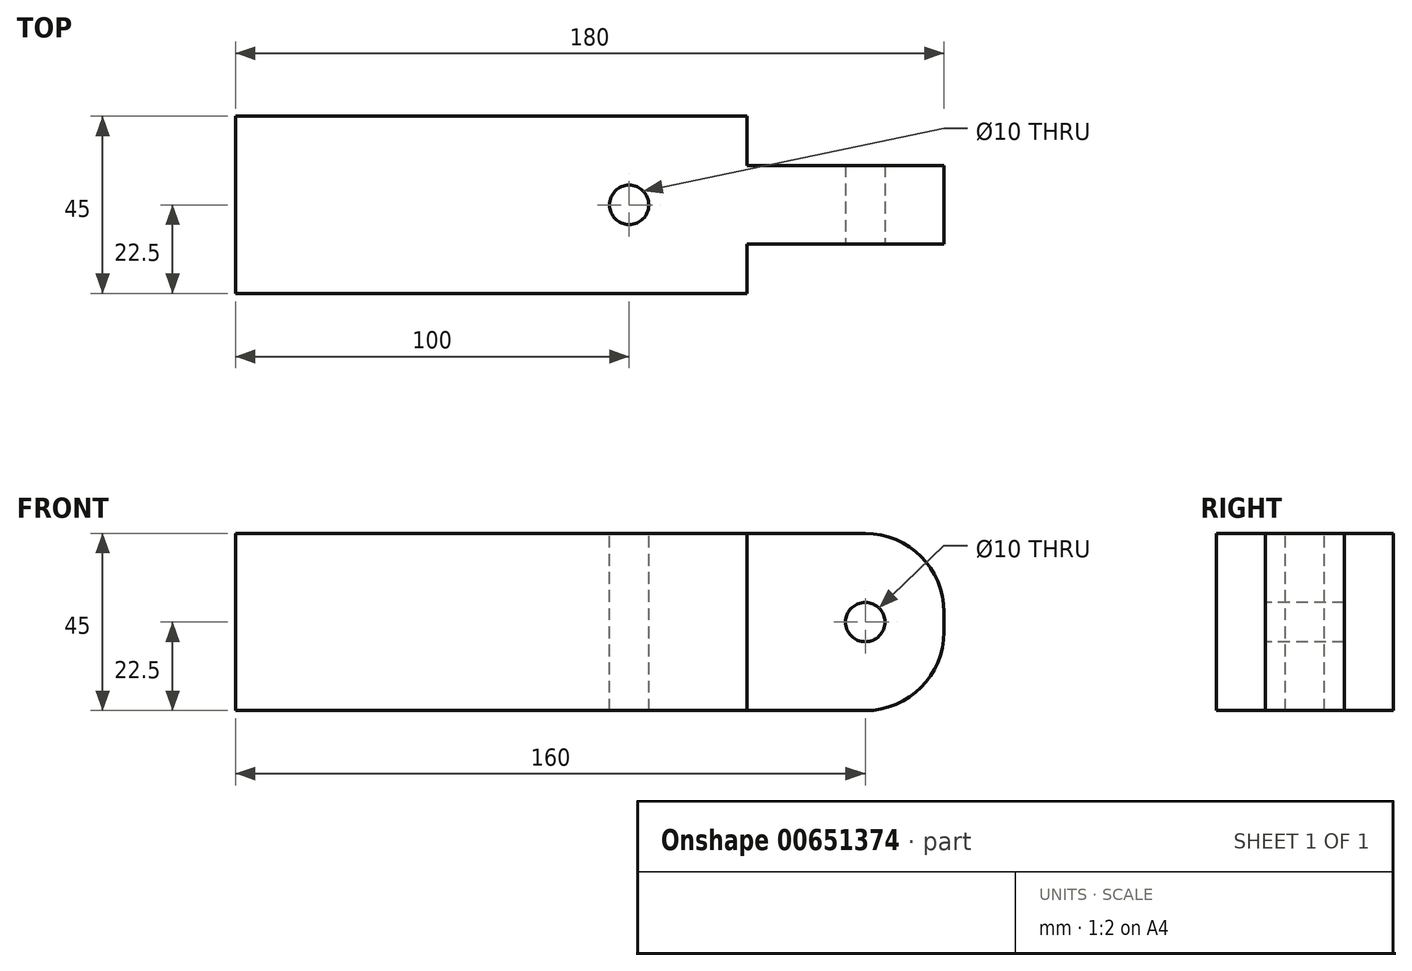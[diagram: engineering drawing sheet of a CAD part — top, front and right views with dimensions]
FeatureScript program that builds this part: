
annotation { "Feature Type Name" : "Feature", "Feature Type Description" : "" }
export const myFeature = defineFeature(function(context is Context, id is Id, definition is map)
    precondition{}
    {
        {
            var Q0;
            Q0=qCreatedBy(makeId("Right.planeOp"),FACE);
            var sketch = newSketch(context, id + "F0", { "sketchPlane" : qUnion([Q0])});
            skLineSegment(sketch, "E0.bottom", {"start": v(0, 0) * mm, "end": v(-45, 0) * mm});
            skLineSegment(sketch, "E0.top", {"start": v(0, 45) * mm, "end": v(-45, 45) * mm});
            skLineSegment(sketch, "E0.left", {"start": v(0, 0) * mm, "end": v(0, 45) * mm});
            skLineSegment(sketch, "E0.right", {"start": v(-45, 0) * mm, "end": v(-45, 45) * mm});
            skSolve(sketch);
        }
        {
            var Q0;
            Q0=makeQuery(id+"F0.imprint","IMPRINT",FACE,{"disambiguationData":[TD([[makeQuery(id+"F0.imprint","IMPRINT",EDGE,{"derivedFrom":sQuery(id+"F0.wireOp",EDGE,"E0.bottom")}),-1.0]])]});
            extrude(context, id + "F1", {"entities" : qUnion([Q0]), "endBound" : BoundingType.SYMMETRIC, "depth" : 130 * mm, "offsetDistance" : 25 * mm});
        }
        {
            var Q0;
            Q0=makeQuery(id+"F1.opExtrude","SWEPT_FACE",FACE,{"disambiguationData":[OSD([sQuery(id+"F0.wireOp",EDGE,"E0.top")])]});
            var sketch = newSketch(context, id + "F2", { "sketchPlane" : qUnion([Q0])});
            skCircle(sketch, "E1", {"center": v(35, -22.5) * mm, "radius": 5 * mm});
            skPoint(sketch, "E1.centerSnap0", {"position": v(65, -22.5) * mm});
            skSolve(sketch);
        }
        {
            var Q0;
            Q0=makeQuery(id+"F2.imprint","IMPRINT",FACE,{"disambiguationData":[TD([[makeQuery(id+"F2.imprint","IMPRINT",EDGE,{"derivedFrom":sQuery(id+"F2.wireOp",EDGE,"E1")}),1.0]])]});
            extrude(context, id + "F3", {"entities" : qUnion([Q0]), "operationType" : NewBodyOperationType.REMOVE, "endBound" : BoundingType.THROUGH_ALL, "oppositeDirection" : true, "depth" : 25 * mm, "offsetDistance" : 25 * mm});
        }
        {
            var Q0;
            Q0=makeQuery(id+"F1.opExtrude","CAP_FACE",FACE,{"disambiguationData":[OSD([sQuery(id+"F0.wireOp",EDGE,"E0.bottom"),sQuery(id+"F0.wireOp",EDGE,"E0.top"),sQuery(id+"F0.wireOp",EDGE,"E0.left"),sQuery(id+"F0.wireOp",EDGE,"E0.right")])],"isStart":false});
            var sketch = newSketch(context, id + "F4", { "sketchPlane" : qUnion([Q0])});
            skLineSegment(sketch, "E2.bottom", {"start": v(-12.5, 45) * mm, "end": v(-32.5, 45) * mm});
            skLineSegment(sketch, "E2.top", {"start": v(-12.5, 0) * mm, "end": v(-32.5, 0) * mm});
            skLineSegment(sketch, "E2.left", {"start": v(-12.5, 45) * mm, "end": v(-12.5, 0) * mm});
            skLineSegment(sketch, "E2.right", {"start": v(-32.5, 45) * mm, "end": v(-32.5, 0) * mm});
            skPoint(sketch, "E2.middle", {"position": v(-22.5, 22.5) * mm});
            skPoint(sketch, "E2.middle.positionSnap0", {"position": v(-22.5, 45) * mm});
            skPoint(sketch, "E2.centerSnap0", {"position": v(-22.5, 45) * mm});
            skSolve(sketch);
        }
        {
            var Q0;
            Q0 = qSketchRegion(id + "F4", true);
            extrude(context, id + "F5", {"entities" : qUnion([Q0]), "operationType" : NewBodyOperationType.ADD, "depth" : 50 * mm, "offsetDistance" : 25 * mm});
        }
        {
            var Q0;
            Q0=makeQuery(id+"F5.opExtrude","CAP_EDGE",EDGE,{"disambiguationData":[OSD([sQuery(id+"F4.wireOp",EDGE,"E2.bottom")])],"isStart":false});
            var Q1;
            Q1=makeQuery(id+"F5.opExtrude","CAP_EDGE",EDGE,{"disambiguationData":[OSD([sQuery(id+"F4.wireOp",EDGE,"E2.top")])],"isStart":false});
            fillet(context, id + "F6", {"entities" : qUnion([Q0, Q1]), "radius" : 20 * mm, "tangentPropagation" : true, "allowEdgeOverflow" : false});
        }
        {
            var Q0;
            Q0=makeQuery(id+"F5.opExtrude","SWEPT_FACE",FACE,{"disambiguationData":[OSD([sQuery(id+"F4.wireOp",EDGE,"E2.right")])]});
            var sketch = newSketch(context, id + "F7", { "sketchPlane" : qUnion([Q0])});
            skCircle(sketch, "E3", {"center": v(95, 22.5) * mm, "radius": 5 * mm});
            skPoint(sketch, "E3.centerSnap0", {"position": v(115, 22.5) * mm});
            skSolve(sketch);
        }
        {
            var Q0;
            Q0 = qSketchRegion(id + "F7", true);
            extrude(context, id + "F8", {"entities" : qUnion([Q0]), "operationType" : NewBodyOperationType.REMOVE, "oppositeDirection" : true, "depth" : 25 * mm, "offsetDistance" : 25 * mm});
        }
    });
